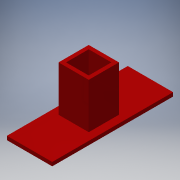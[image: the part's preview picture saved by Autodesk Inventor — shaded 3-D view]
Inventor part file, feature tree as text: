
AUTODESK INVENTOR PART (.ipt)
format: ipt  version: 2016 (Build 200138000, 138)  size: 113,152 bytes
history: native  units: in
note: dims shown in document units (in); Inventor stores cm internally (conversion verified against a paired STEP export)
features: extrude x3, sketch x2
ambient origin geometry x8: Origin, YZ Plane, XZ Plane, XY Plane, X Axis, Y Axis, Z Axis, Center Point
bodies: Solid1 (feature_tree)
feature tree (5):
  extrude  "Extrusion1"  Depth=4.0in
  sketch  "Sketch3"  dims[d2=0.125in d3=0.0in d8=1.0in d9=1.0in d10=0.25in d11=1.542in d12=0.125in d13=1.5in d14=0.0in d15=0.2in d16=0.5in d17=0.5in d20=0.125in d21=0.0in]
  extrude  "Extrusion3"  Depth=1.0in
  extrude  "Extrusion5"  Depth=1.0in
  sketch  "Sketch1"  dims[d0=1.5in d1=4.0in]
